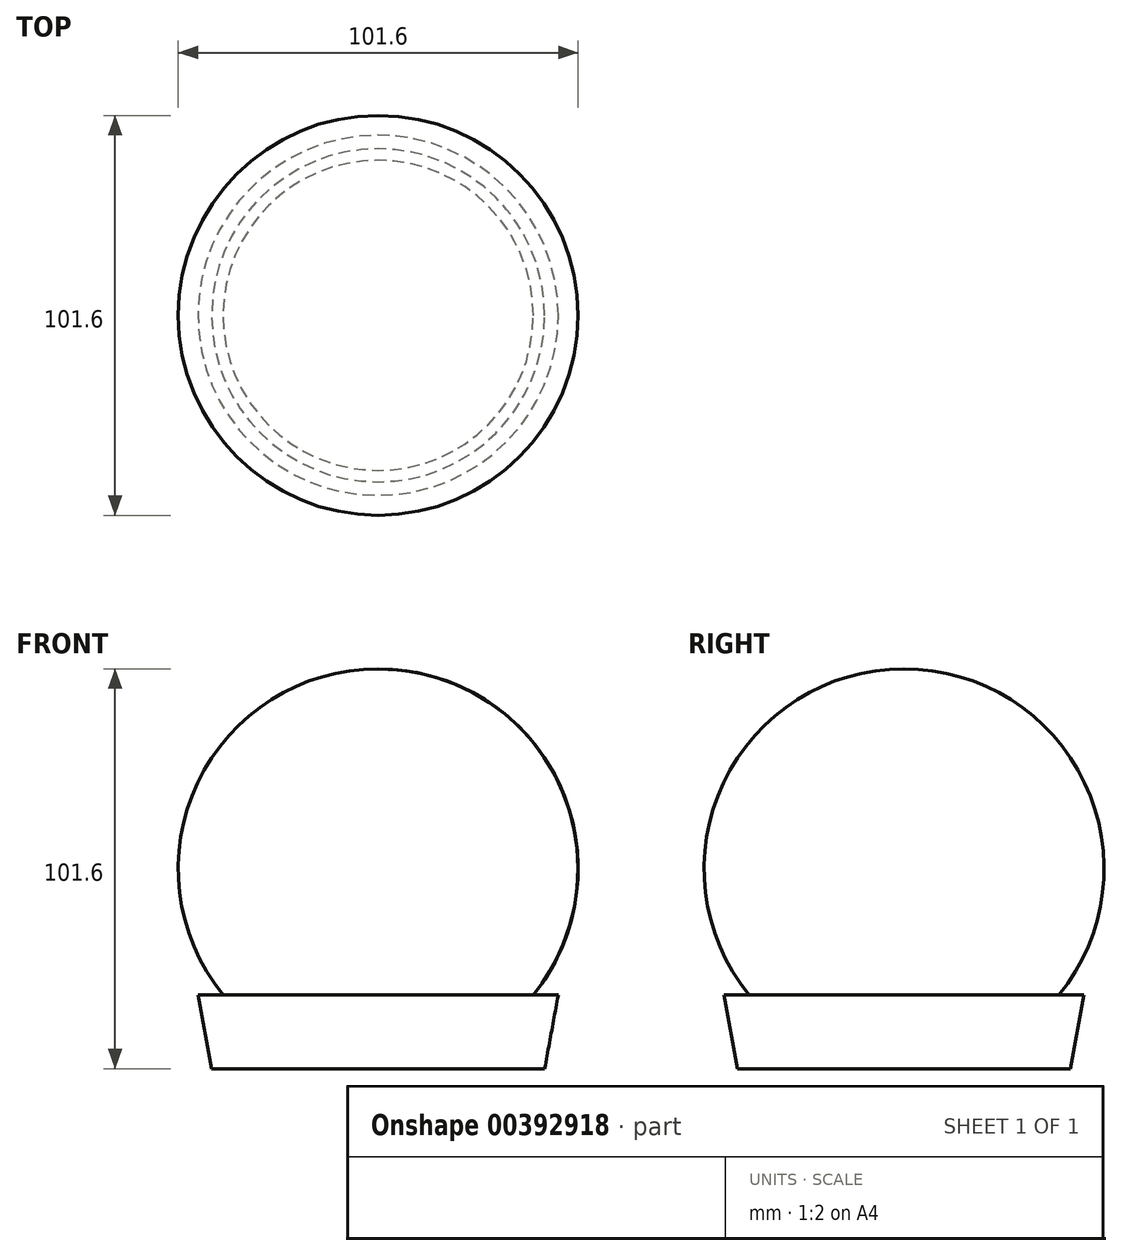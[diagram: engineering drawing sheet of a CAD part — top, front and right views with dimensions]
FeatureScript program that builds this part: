
annotation { "Feature Type Name" : "Feature", "Feature Type Description" : "" }
export const myFeature = defineFeature(function(context is Context, id is Id, definition is map)
    precondition{}
    {
        {
            var Q0;
            Q0=qCreatedBy(makeId("Front.planeOp"),FACE);
            var sketch = newSketch(context, id + "F0", { "sketchPlane" : qUnion([Q0])});
            skArc(sketch, "E0", {"start": v(0, 50.8) * mm, "mid": v(-45.88, 21.81) * mm, "end": v(-39.4, -32.06) * mm});
            skLineSegment(sketch, "E1", {"start": v(0, 0) * mm, "end": v(0, 50.8) * mm});
            skLineSegment(sketch, "E2", {"start": v(0, 0) * mm, "end": v(0, -50.8) * mm});
            skLineSegment(sketch, "E3", {"start": v(-39.4, -32.06) * mm, "end": v(-45.75, -32.06) * mm});
            skLineSegment(sketch, "E4", {"start": v(-45.75, -32.06) * mm, "end": v(-42.3, -50.8) * mm});
            skLineSegment(sketch, "E5", {"start": v(-42.3, -50.8) * mm, "end": v(-35.95, -50.8) * mm});
            skLineSegment(sketch, "E6", {"start": v(-37.5, -50.8) * mm, "end": v(-37.48, -51.02) * mm});
            skLineSegment(sketch, "E7", {"start": v(-35.95, -50.8) * mm, "end": v(0, -50.8) * mm});
            skSolve(sketch);
        }
        {
            var Q0;
            Q0 = qSketchRegion(id + "F0", true);
            var Q1;
            Q1=sQuery(id+"F0.wireOp",EDGE,"E2");
            revolve(context, id + "F1", {"entities" : qUnion([Q0]), "axis" : qUnion([Q1]), "revolveType" : RevolveType.FULL});
        }
    });
